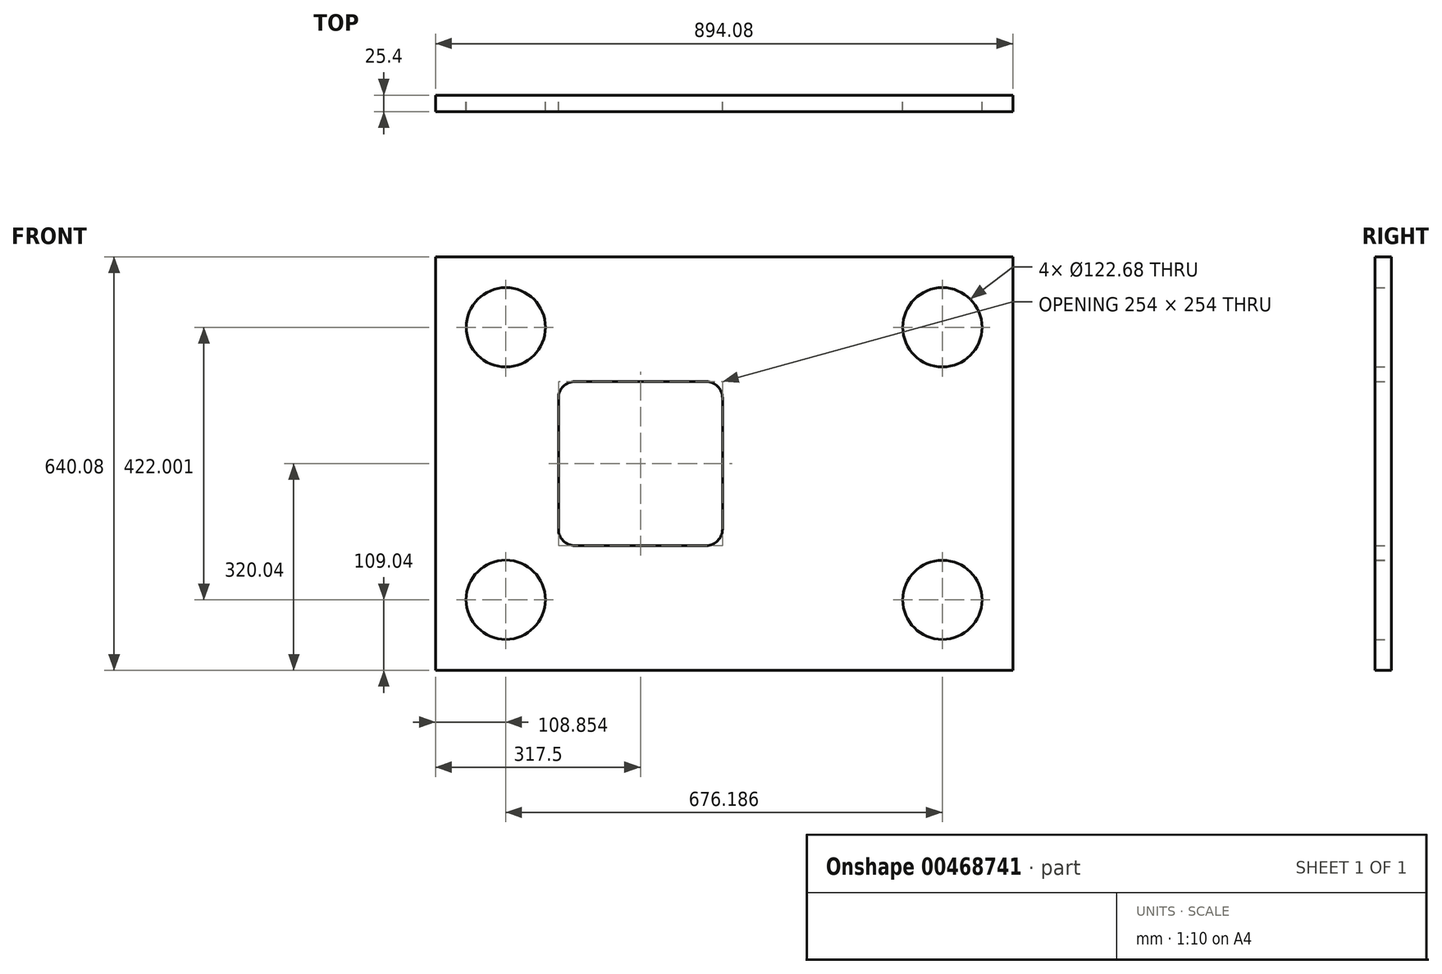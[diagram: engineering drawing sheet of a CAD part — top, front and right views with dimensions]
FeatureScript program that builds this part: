
annotation { "Feature Type Name" : "Feature", "Feature Type Description" : "" }
export const myFeature = defineFeature(function(context is Context, id is Id, definition is map)
    precondition{}
    {
        {
            var Q0;
            Q0=qCreatedBy(makeId("Front.planeOp"),FACE);
            var sketch = newSketch(context, id + "F0", { "sketchPlane" : qUnion([Q0])});
            skLineSegment(sketch, "E0", {"start": v(447.04, -320.04) * mm, "end": v(-447.04, -320.04) * mm});
            skLineSegment(sketch, "E1", {"start": v(-447.04, -320.04) * mm, "end": v(-447.04, 320.04) * mm});
            skCircle(sketch, "E2", {"center": v(-338, 211) * mm, "radius": 61.34 * mm});
            skCircle(sketch, "E3", {"center": v(338, 211) * mm, "radius": 61.34 * mm});
            skCircle(sketch, "E4", {"center": v(338, -211) * mm, "radius": 61.34 * mm});
            skCircle(sketch, "E5", {"center": v(-338.19, -210.81) * mm, "radius": 61.34 * mm});
            skLineSegment(sketch, "E6", {"start": v(-447.04, 320.04) * mm, "end": v(447.04, 320.04) * mm});
            skLineSegment(sketch, "E7", {"start": v(447.04, 320.04) * mm, "end": v(447.04, -320.04) * mm});
            skLineSegment(sketch, "E8", {"start": v(-2.54, 101.6) * mm, "end": v(-2.54, -101.6) * mm});
            skLineSegment(sketch, "E9", {"start": v(-27.94, -127) * mm, "end": v(-231.14, -127) * mm});
            skLineSegment(sketch, "E10", {"start": v(-256.54, -101.6) * mm, "end": v(-256.54, 101.6) * mm});
            skLineSegment(sketch, "E11", {"start": v(-231.14, 127) * mm, "end": v(-27.94, 127) * mm});
            skArc(sketch, "E12", {"start": v(-231.14, 127) * mm, "mid": v(-249.1, 119.56) * mm, "end": v(-256.54, 101.6) * mm});
            skArc(sketch, "E13", {"start": v(-2.54, 101.6) * mm, "mid": v(-9.98, 119.56) * mm, "end": v(-27.94, 127) * mm});
            skArc(sketch, "E14", {"start": v(-27.94, -127) * mm, "mid": v(-9.98, -119.56) * mm, "end": v(-2.54, -101.6) * mm});
            skArc(sketch, "E15", {"start": v(-256.54, -101.6) * mm, "mid": v(-249.1, -119.56) * mm, "end": v(-231.14, -127) * mm});
            skSolve(sketch);
        }
        {
            var Q0;
            Q0=makeQuery(id+"F0.imprint","IMPRINT",FACE,{"disambiguationData":[TD([[makeQuery(id+"F0.imprint","IMPRINT",EDGE,{"derivedFrom":sQuery(id+"F0.wireOp",EDGE,"E0")}),-1.0]])]});
            extrude(context, id + "F1", {"entities" : qUnion([Q0]), "depth" : 25.4 * mm});
        }
    });
